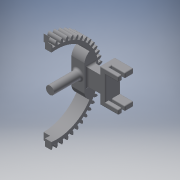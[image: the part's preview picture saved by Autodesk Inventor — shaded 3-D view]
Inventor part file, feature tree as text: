
AUTODESK INVENTOR PART (.ipt)
format: ipt  version: 2018 (Build 220112000, 112)  size: 1,059,328 bytes
history: native  units: in
note: dims shown in document units (in); Inventor stores cm internally (conversion verified against a paired STEP export)
features: extrude x23, sketch x22, fillet x5, other x2, plane x1
ambient origin geometry x8: Origin, YZ Plane, XZ Plane, XY Plane, X Axis, Y Axis, Z Axis, Center Point
bodies: Body1 (feature_tree)
feature tree (53):
  other  "main sketch"
  extrude  "teeth extrude"  Depth=3.25in
  extrude  "other teeth extrude"  Depth=1.2025in
  extrude  "servo holder extrude"  Depth=0.5in TaperAngle=0.0deg
  fillet  "servo fillet"  Radius=0.5in
  extrude  "Extrusion10"  Depth=0.5in
  other  "axel work plane"
  plane  "Work Plane7"
  sketch  "Sketch10"  dims[d7=1.2025in d8=1.2025in]
  extrude  "Extrusion18"  Depth=0.15in
  extrude  "Extrusion19"  Depth=0.0039in
  extrude  "Extrusion21"  Depth=0.2in
  extrude  "Extrusion23"  Depth=0.25in
  extrude  "Extrusion25"  Depth=0.3937in TaperAngle=0.0deg
  extrude  "Extrusion26"  Depth=0.3937in TaperAngle=0.0deg
  extrude  "Extrusion30"  Depth=1.3125in TaperAngle=0.0deg
  extrude  "Extrusion33"  Depth=0.33in TaperAngle=0.0deg
  extrude  "Extrusion35"  Depth=0.0375in TaperAngle=0.0deg
  extrude  "Extrusion36"  Depth=0.106in
  sketch  "Sketch34"  dims[d124=0.05in d125=0.0in d128=0.0375in d129=0.0in]
  extrude  "Extrusion38"  Depth=0.1in
  sketch  "Sketch37"  dims[d136=0.5in d137=0.0in d140=0.1in]
  extrude  "Extrusion40"  Depth=0.5in TaperAngle=0.0deg
  extrude  "Extrusion41"  Depth=0.2in
  extrude  "Extrusion42"  Depth=0.2in TaperAngle=0.0deg
  extrude  "Extrusion43"  Depth=0.2in TaperAngle=0.0deg
  extrude  "Extrusion44"  Depth=0.2in TaperAngle=0.0deg
  extrude  "Extrusion45"  Depth=0.0787in
  extrude  "Extrusion47"  Depth=0.0394in
  extrude  "Extrusion48"  Depth=0.0394in
  fillet  "Fillet4"  [1 undecoded]
  fillet  "Fillet5"  [1 undecoded]
  fillet  "Fillet6"  [1 undecoded]
  fillet  "Fillet7"  [1 undecoded]
  sketch  "Sketch5"  dims[d0=3.0in d1=3.25in]
  sketch  "Sketch11"  dims[d13=20.4724in d15=360.0deg d19=0.5in d20=0.0in d23=0.5in d24=0.0in]
  sketch  "Sketch13"  dims[d45=0.5in d46=0.0in d48=0.1875in]
  sketch  "Sketch14"  dims[d53=0.15in d56=0.0039in]
  sketch  "Sketch17"  dims[d57=0.0591in d58=0.0039in]
  sketch  "Sketch19"  dims[d59=0.2in d60=0.0in d73=0.0025in]
  sketch  "Sketch20"  dims[d78=0.1969in d79=0.25in]
  sketch  "Sketch26"  dims[d80=39.3701in d81=19.685in d82=0.0in d83=0.0in d85=0.3937in d86=0.0in]
  sketch  "Sketch30"  dims[d88=0.311in d91=0.3937in d92=0.0in]
  sketch  "Sketch32"  dims[d97=2.0in d98=0.0in d102=1.3125in d103=0.0in]
  sketch  "Sketch33"  dims[d104=1.3125in d105=0.0in d118=0.33in d119=0.0in]
  sketch  "Sketch36"  dims[d130=0.0188in d131=0.0in d135=0.106in]
  sketch  "Sketch38"  dims[d141=0.15in d142=0.5in d143=0.0in]
  sketch  "Sketch39"  dims[d144=0.9in d145=0.2in]
  sketch  "Sketch40"  dims[d146=0.5in d147=0.0in d148=0.2in d149=0.0in]
  sketch  "Sketch41"  dims[d150=0.2in d151=0.0in d152=0.2in d153=0.0in]
  sketch  "Sketch42"  dims[d154=0.2in d155=0.0in d158=0.0125in d159=0.0in]
  sketch  "Sketch43"  dims[d160=0.0125in d161=0.0in d162=0.0787in]
  sketch  "Sketch45"  dims[d165=0.0394in d166=0.0394in d167=0.0394in]
note: 4 required parameter values undecoded (feature->parameter linkage not recoverable at this tier; creation-order binding heuristic only, values carry confidence <= 0.55)
